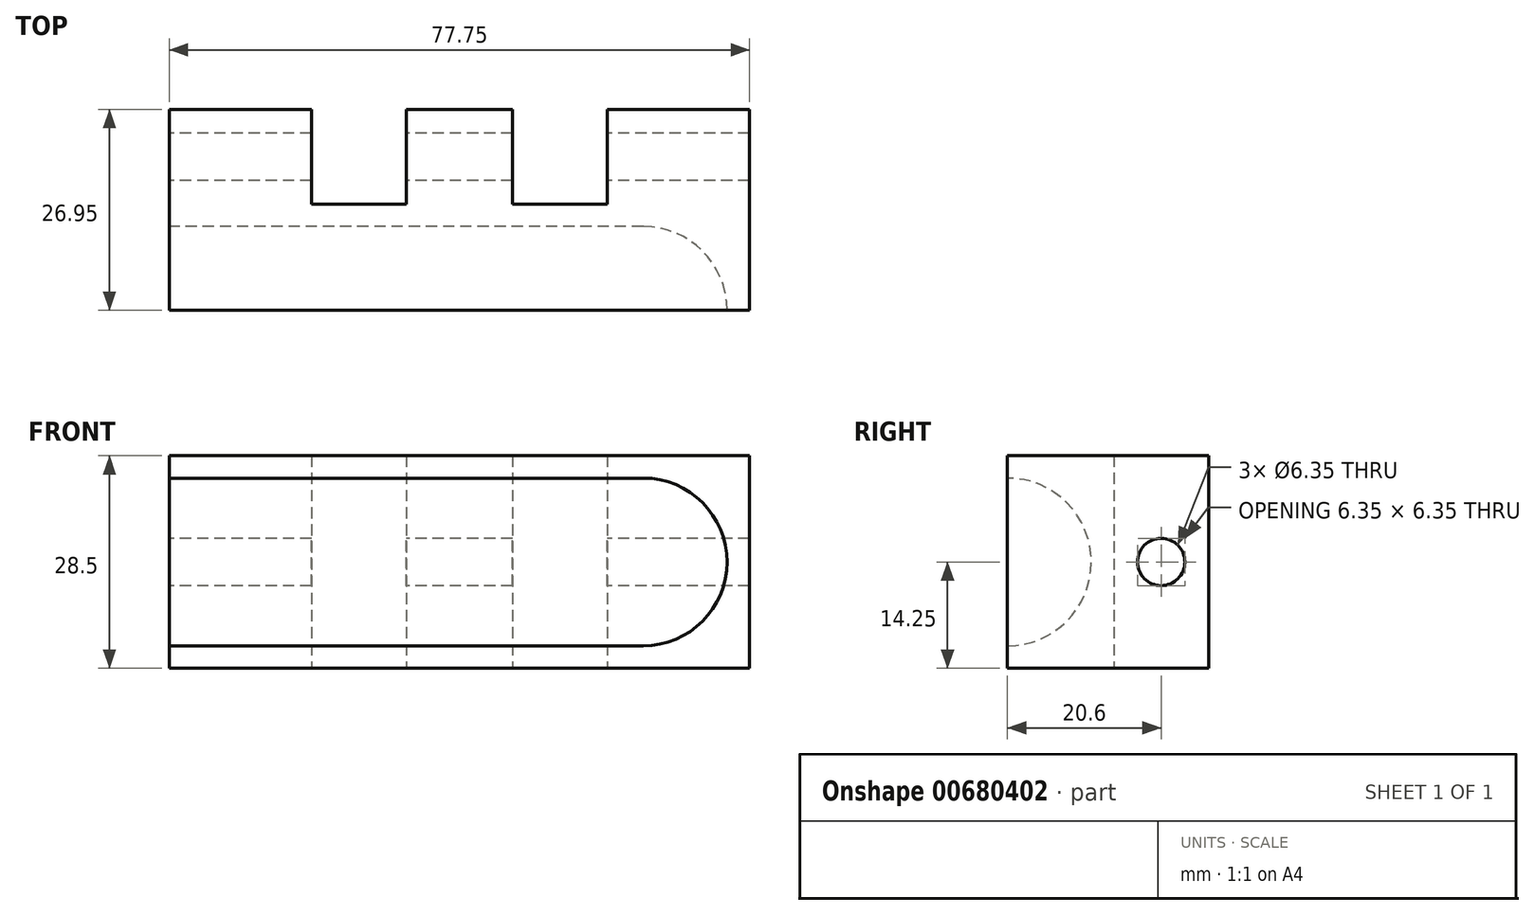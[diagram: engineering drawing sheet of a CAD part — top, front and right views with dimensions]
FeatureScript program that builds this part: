
annotation { "Feature Type Name" : "Feature", "Feature Type Description" : "" }
export const myFeature = defineFeature(function(context is Context, id is Id, definition is map)
    precondition{}
    {
        {
            var Q0;
            Q0=qCreatedBy(makeId("Front.planeOp"),FACE);
            var sketch = newSketch(context, id + "F0", { "sketchPlane" : qUnion([Q0])});
            skArc(sketch, "E0", {"start": v(31.75, -11.25) * mm, "mid": v(39.7, -7.95) * mm, "end": v(43, 0) * mm});
            skLineSegment(sketch, "E1", {"start": v(0, 11.25) * mm, "end": v(0, -11.25) * mm, "construction": true});
            skLineSegment(sketch, "E2", {"start": v(0, 0) * mm, "end": v(56, 0) * mm, "construction": true});
            skLineSegment(sketch, "E3", {"start": v(31.75, -11.25) * mm, "end": v(0, -11.25) * mm});
            skPoint(sketch, "E4.MirrorCS.end.orphan", {"position": v(0, 11.25) * mm});
            skPoint(sketch, "E5.MirrorCS.end.orphan", {"position": v(0, -11.25) * mm});
            skLineSegment(sketch, "E6.MirrorCS", {"start": v(-31.75, -11.25) * mm, "end": v(0, -11.25) * mm});
            skLineSegment(sketch, "E7", {"start": v(-31.75, -14.25) * mm, "end": v(-31.75, -11.25) * mm});
            skLineSegment(sketch, "E8", {"start": v(-31.75, -14.25) * mm, "end": v(31.75, -14.25) * mm});
            skArc(sketch, "E9", {"start": v(31.75, -14.25) * mm, "mid": v(41.83, -10.08) * mm, "end": v(46, 0) * mm});
            skLineSegment(sketch, "E10", {"start": v(43, 0) * mm, "end": v(46, 0) * mm});
            skSolve(sketch);
        }
        {
            var Q0;
            Q0=qSketchRegion(id+"F0",true);
            var Q1;
            Q1=sQuery(id+"F0.wireOp",EDGE,"E2");
            revolve(context, id + "F1", {"entities" : qUnion([Q0]), "axis" : qUnion([Q1]), "revolveType" : RevolveType.ONE_DIRECTION, "angle" : 180 * degree});
        }
        {
            var Q0;
            Q0=qCreatedBy(makeId("Right.planeOp"),FACE);
            var sketch = newSketch(context, id + "F2", { "sketchPlane" : qUnion([Q0])});
            skLineSegment(sketch, "E11", {"start": v(26.95, -8.53) * mm, "end": v(26.95, 11.07) * mm});
            skSolve(sketch);
        }
        {
            var Q0;
            Q0=qBodyType(qCreatedBy(id+"F2",EDGE),BodyType.WIRE);
            var Q1;
            Q1=qCreatedBy(makeId("Front.planeOp"),FACE);
            cPlane(context, id + "F3", {"entities" : qUnion([Q0, Q1]), "cplaneType" : CPlaneType.LINE_ANGLE, "offset" : 25.4 * mm, "angle" : 0 * degree, "width" : 152.4 * mm, "height" : 152.4 * mm});
        }
        {
            var Q0;
            Q0=qCreatedBy(id+"F3.planeOp",FACE);
            var sketch = newSketch(context, id + "F4", { "sketchPlane" : qUnion([Q0])});
            skLineSegment(sketch, "E12.MirrorCS", {"start": v(-46, 14.25) * mm, "end": v(31.75, 14.25) * mm});
            skLineSegment(sketch, "E13.MirrorCS", {"start": v(-46, -14.25) * mm, "end": v(-46, 14.25) * mm});
            skLineSegment(sketch, "E14.MirrorCS", {"start": v(31.75, -14.25) * mm, "end": v(31.75, 14.25) * mm});
            skLineSegment(sketch, "E15.MirrorCS", {"start": v(-46, -14.25) * mm, "end": v(31.75, -14.25) * mm});
            skLineSegment(sketch, "E16", {"start": v(-46, 0) * mm, "end": v(-46, -20.05) * mm, "construction": true});
            skSolve(sketch);
        }
        {
            var Q0;
            Q0=makeQuery(id+"F4.imprint","IMPRINT",FACE,{"disambiguationData":[TD([[makeQuery(id+"F4.imprint","IMPRINT",EDGE,{"derivedFrom":sQuery(id+"F4.wireOp",EDGE,"E12.MirrorCS")}),-1.0]])]});
            var Q1;
            Q1=makeQuery(id+"F4.imprint","IMPRINT",FACE,{"disambiguationData":[TD([[makeQuery(id+"F4.imprint","IMPRINT",EDGE,{"derivedFrom":sQuery(id+"F4.wireOp",EDGE,"n8HN8Yoi-FMpD-m4Aa-9D2k-B1jSctUaQO8O.bottom")}),1.0]])]});
            var Q2;
            Q2=makeQuery(id+"F1.opRevolve","SWEPT_FACE",FACE,{"disambiguationData":[OSD([sQuery(id+"F0.wireOp",EDGE,"E8")])]});
            extrude(context, id + "F5", {"entities" : qUnion([Q0, Q1]), "operationType" : NewBodyOperationType.ADD, "endBound" : BoundingType.UP_TO_SURFACE, "oppositeDirection" : true, "depth" : 25.4 * mm, "endBoundEntityFace" : qUnion([Q2]), "offsetDistance" : 25.4 * mm});
        }
        {
            var Q0;
            Q0=makeQuery(id+"F5.opExtrude","SWEPT_FACE",FACE,{"disambiguationData":[OSD([sQuery(id+"F4.wireOp",EDGE,"c5c998f1-e7e6-4946-a863-416f278517182.MirrorCS"),sQuery(id+"F4.wireOp",EDGE,"E14.MirrorCS")])]});
            var sketch = newSketch(context, id + "F6", { "sketchPlane" : qUnion([Q0])});
            skLineSegment(sketch, "E17", {"start": v(-26.95, 0) * mm, "end": v(-20.6, 0) * mm, "construction": true});
            skCircle(sketch, "E18", {"center": v(-20.6, 0) * mm, "radius": 3.18 * mm});
            skSolve(sketch);
        }
        {
            var Q0;
            Q0=qSketchRegion(id+"F6",true);
            extrude(context, id + "F7", {"entities" : qUnion([Q0]), "operationType" : NewBodyOperationType.REMOVE, "endBound" : BoundingType.THROUGH_ALL, "oppositeDirection" : true, "depth" : 25.4 * mm, "offsetDistance" : 25.4 * mm});
        }
        {
            var Q0;
            Q0=makeQuery(id+"F5.opExtrude","SWEPT_FACE",FACE,{"disambiguationData":[OSD([sQuery(id+"F4.wireOp",EDGE,"E13.MirrorCS")])]});
            var sketch = newSketch(context, id + "F8", { "sketchPlane" : qUnion([Q0])});
            skArc(sketch, "E19.0", {"start": v(0, 14.25) * mm, "mid": v(14.25, 0) * mm, "end": v(0, -14.25) * mm});
            skLineSegment(sketch, "E20.0", {"start": v(0, 14.25) * mm, "end": v(0, -14.25) * mm});
            skSolve(sketch);
        }
        {
            var Q0;
            Q0=makeQuery(id+"F8.imprint","IMPRINT",FACE,{"disambiguationData":[TD([[makeQuery(id+"F8.imprint","IMPRINT",EDGE,{"derivedFrom":sQuery(id+"F8.wireOp",EDGE,"E19.0")}),-1.0]])]});
            var Q1;
            Q1=makeQuery(id+"F1.opRevolve","SWEPT_FACE",FACE,{"disambiguationData":[OSD([sQuery(id+"F0.wireOp",EDGE,"E9")])]});
            var Q2;
            Q2=makeQuery(id+"F1.opRevolve","SWEPT_BODY",BODY,{"disambiguationData":[OSD([sQuery(id+"F0.wireOp",EDGE,"E0"),sQuery(id+"F0.wireOp",EDGE,"E3"),sQuery(id+"F0.wireOp",EDGE,"E6.MirrorCS"),sQuery(id+"F0.wireOp",EDGE,"E7"),sQuery(id+"F0.wireOp",EDGE,"E8"),sQuery(id+"F0.wireOp",EDGE,"E9"),sQuery(id+"F0.wireOp",EDGE,"E10")])]});
            extrude(context, id + "F9", {"entities" : qUnion([Q0]), "operationType" : NewBodyOperationType.ADD, "endBound" : BoundingType.UP_TO_SURFACE, "oppositeDirection" : true, "depth" : 25.4 * mm, "endBoundEntityFace" : qUnion([Q1]), "endBoundEntityBody" : qUnion([Q2]), "offsetDistance" : 25.4 * mm});
        }
        {
            var Q0;
            Q0=makeQuery(id+"F5.opExtrude","SWEPT_FACE",FACE,{"disambiguationData":[OSD([sQuery(id+"F4.wireOp",EDGE,"E15.MirrorCS")])]});
            var sketch = newSketch(context, id + "F10", { "sketchPlane" : qUnion([Q0])});
            skLineSegment(sketch, "E21.bottom", {"start": v(26.95, -26.95) * mm, "end": v(14.25, -26.95) * mm});
            skLineSegment(sketch, "E21.top", {"start": v(26.95, -14.25) * mm, "end": v(14.25, -14.25) * mm});
            skLineSegment(sketch, "E21.left", {"start": v(26.95, -26.95) * mm, "end": v(26.95, -14.25) * mm});
            skLineSegment(sketch, "E21.right", {"start": v(14.25, -26.95) * mm, "end": v(14.25, -14.25) * mm});
            skLineSegment(sketch, "E22.bottom", {"start": v(0, -26.95) * mm, "end": v(-12.7, -26.95) * mm});
            skLineSegment(sketch, "E22.top", {"start": v(0, -14.25) * mm, "end": v(-12.7, -14.25) * mm});
            skLineSegment(sketch, "E22.left", {"start": v(0, -26.95) * mm, "end": v(0, -14.25) * mm});
            skLineSegment(sketch, "E22.right", {"start": v(-12.7, -26.95) * mm, "end": v(-12.7, -14.25) * mm});
            skSolve(sketch);
        }
        {
            var Q0;
            Q0 = qSketchRegion(id + "F10", true);
            extrude(context, id + "F11", {"entities" : qUnion([Q0]), "operationType" : NewBodyOperationType.REMOVE, "endBound" : BoundingType.THROUGH_ALL, "oppositeDirection" : true, "depth" : 25.4 * mm, "offsetDistance" : 25.4 * mm});
        }
    });
